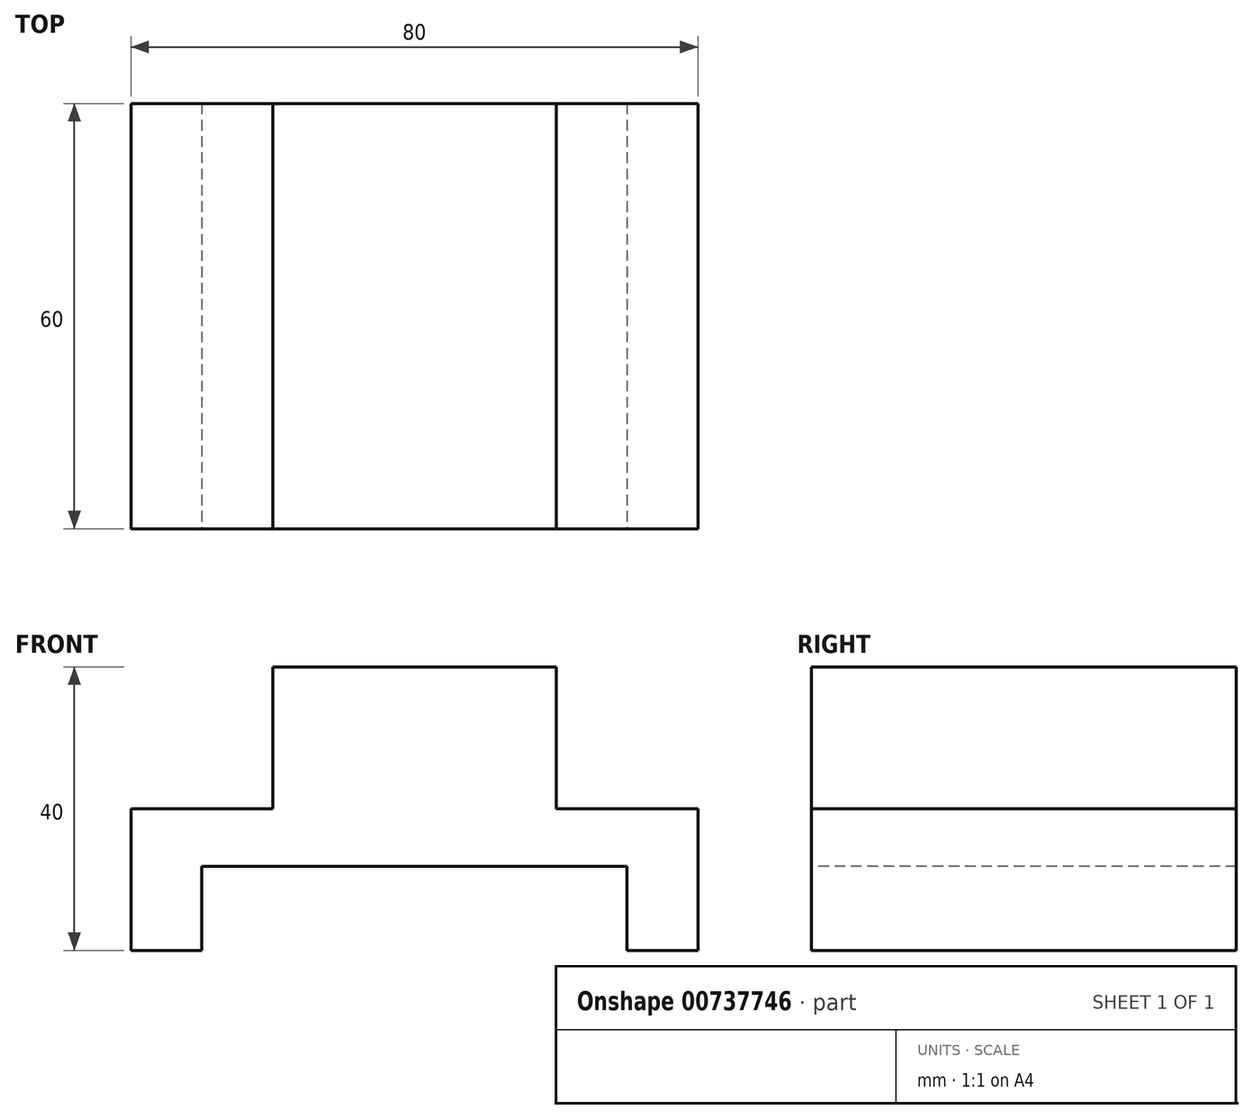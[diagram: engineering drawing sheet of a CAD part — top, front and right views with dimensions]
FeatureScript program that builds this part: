
annotation { "Feature Type Name" : "Feature", "Feature Type Description" : "" }
export const myFeature = defineFeature(function(context is Context, id is Id, definition is map)
    precondition{}
    {
        {
            var Q0;
            Q0=qCreatedBy(makeId("Front.planeOp"),FACE);
            var sketch = newSketch(context, id + "F0", { "sketchPlane" : qUnion([Q0])});
            skLineSegment(sketch, "E0", {"start": v(0, 0) * mm, "end": v(10, 0) * mm});
            skLineSegment(sketch, "E1", {"start": v(10, 0) * mm, "end": v(10, 11.82) * mm});
            skLineSegment(sketch, "E2", {"start": v(10, 11.82) * mm, "end": v(70, 11.82) * mm});
            skLineSegment(sketch, "E3", {"start": v(70, 11.82) * mm, "end": v(70, 0) * mm});
            skLineSegment(sketch, "E4", {"start": v(70, 0) * mm, "end": v(80, 0) * mm});
            skLineSegment(sketch, "E5", {"start": v(80, 0) * mm, "end": v(80, 20) * mm});
            skLineSegment(sketch, "E6", {"start": v(80, 20) * mm, "end": v(60, 20) * mm});
            skLineSegment(sketch, "E7", {"start": v(60, 20) * mm, "end": v(60, 40) * mm});
            skLineSegment(sketch, "E8", {"start": v(60, 40) * mm, "end": v(20, 40) * mm});
            skLineSegment(sketch, "E9", {"start": v(20, 40) * mm, "end": v(20, 20) * mm});
            skLineSegment(sketch, "E10", {"start": v(20, 20) * mm, "end": v(0, 20) * mm});
            skLineSegment(sketch, "E11", {"start": v(0, 20) * mm, "end": v(0, 0) * mm});
            skSolve(sketch);
        }
        {
            var Q0;
            Q0 = qSketchRegion(id + "F0", true);
            extrude(context, id + "F1", {"entities" : qUnion([Q0]), "oppositeDirection" : true, "depth" : 60 * mm, "offsetDistance" : 25 * mm});
        }
    });
